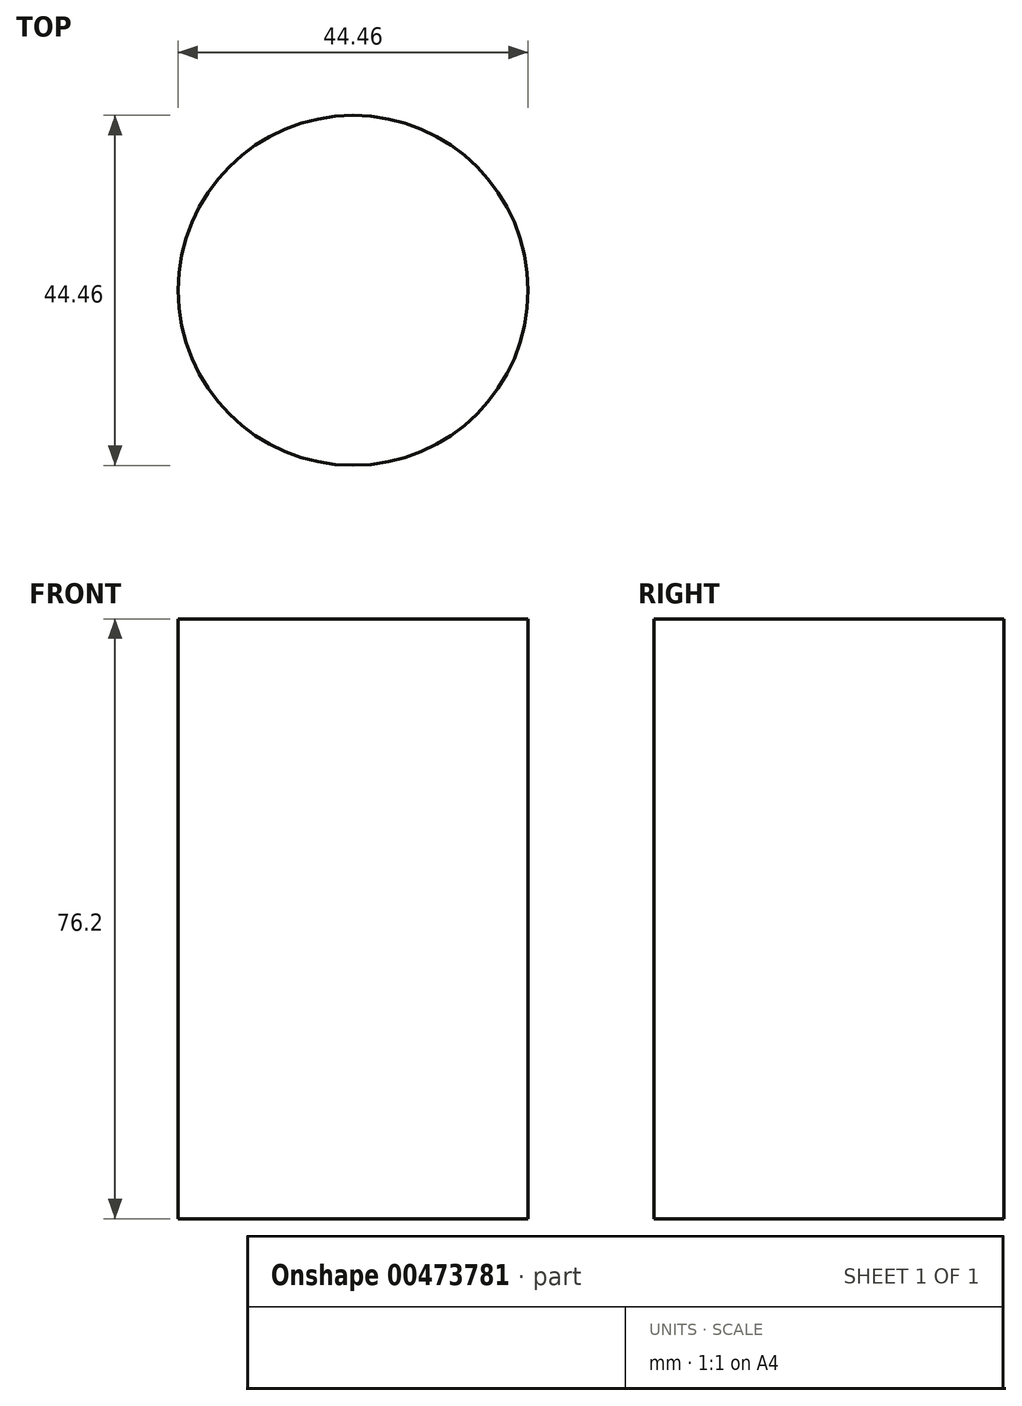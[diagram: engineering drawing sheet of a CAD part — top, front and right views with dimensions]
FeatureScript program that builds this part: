
annotation { "Feature Type Name" : "Feature", "Feature Type Description" : "" }
export const myFeature = defineFeature(function(context is Context, id is Id, definition is map)
    precondition{}
    {
        {
            var Q0;
            Q0=qCreatedBy(makeId("Top.planeOp"),FACE);
            var sketch = newSketch(context, id + "F0", { "sketchPlane" : qUnion([Q0])});
            skCircle(sketch, "E0", {"center": v(0, 0) * mm, "radius": 22.23 * mm});
            skSolve(sketch);
        }
        {
            var Q0;
            Q0 = qSketchRegion(id + "F0", true);
            extrude(context, id + "F1", {"entities" : qUnion([Q0]), "depth" : 76.2 * mm});
        }
    });
